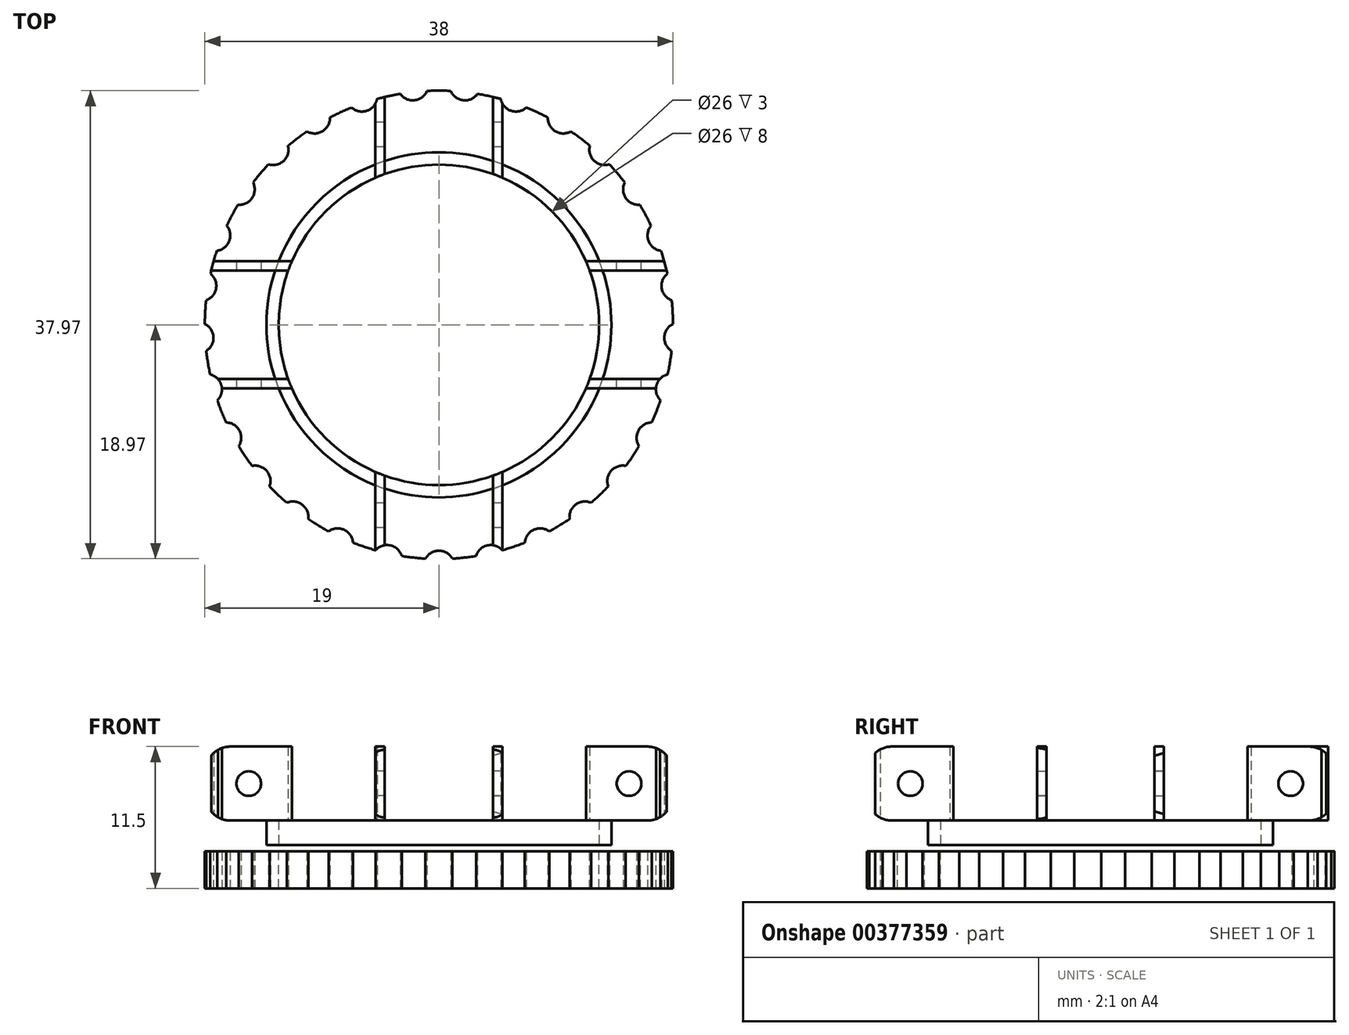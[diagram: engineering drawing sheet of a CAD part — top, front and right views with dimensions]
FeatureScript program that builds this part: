
annotation { "Feature Type Name" : "Feature", "Feature Type Description" : "" }
export const myFeature = defineFeature(function(context is Context, id is Id, definition is map)
    precondition{}
    {
        {
            var Q0;
            Q0=qCreatedBy(makeId("Top.planeOp"),FACE);
            var sketch = newSketch(context, id + "F0", { "sketchPlane" : qUnion([Q0])});
            skCircle(sketch, "E0", {"center": v(0, 0) * mm, "radius": 11 * mm});
            skArc(sketch, "E1.0", {"start": v(-5.15, 11.93) * mm, "mid": v(-9.2, 9.2) * mm, "end": v(-11.93, 5.15) * mm});
            skLineSegment(sketch, "E2.bottom", {"start": v(-4.4, 18.93) * mm, "end": v(-5.8, 18.93) * mm});
            skLineSegment(sketch, "E2.top", {"start": v(-4.4, 18.93) * mm, "end": v(-5.8, 18.93) * mm});
            skLineSegment(sketch, "E2.left", {"start": v(-4.4, 18.93) * mm, "end": v(-4.4, 18.93) * mm});
            skLineSegment(sketch, "E2.right", {"start": v(-5.8, 18.93) * mm, "end": v(-5.8, 18.93) * mm});
            skLineSegment(sketch, "E3.bottom", {"start": v(-4.4, 18.93) * mm, "end": v(-5.15, 18.93) * mm});
            skLineSegment(sketch, "E3.left", {"start": v(-4.4, 18.93) * mm, "end": v(-4.4, 12.23) * mm});
            skLineSegment(sketch, "E3.right", {"start": v(-5.15, 18.93) * mm, "end": v(-5.15, 11.93) * mm});
            skLineSegment(sketch, "E4.bottom", {"start": v(5.15, 18.93) * mm, "end": v(4.4, 18.93) * mm});
            skLineSegment(sketch, "E4.left", {"start": v(5.15, 18.93) * mm, "end": v(5.15, 11.93) * mm});
            skLineSegment(sketch, "E4.right", {"start": v(4.4, 18.93) * mm, "end": v(4.4, 12.23) * mm});
            skPoint(sketch, "E5.orphan", {"position": v(-5.15, 11.36) * mm});
            skArc(sketch, "E6.trimOffspring", {"start": v(4.4, 12.23) * mm, "mid": v(0, 13) * mm, "end": v(-4.4, 12.23) * mm});
            skPoint(sketch, "E4.top.end.orphan", {"position": v(4.4, 11.36) * mm});
            skLineSegment(sketch, "E7.bottom", {"start": v(-18.93, 5.15) * mm, "end": v(-11.93, 5.15) * mm});
            skLineSegment(sketch, "E7.top", {"start": v(-18.93, 4.4) * mm, "end": v(-12.23, 4.4) * mm});
            skLineSegment(sketch, "E7.left", {"start": v(-18.93, 5.15) * mm, "end": v(-18.93, 4.4) * mm});
            skLineSegment(sketch, "E8.bottom", {"start": v(-18.93, -5.15) * mm, "end": v(-11.93, -5.15) * mm});
            skLineSegment(sketch, "E8.top", {"start": v(-18.93, -4.4) * mm, "end": v(-12.23, -4.4) * mm});
            skLineSegment(sketch, "E8.left", {"start": v(-18.93, -5.15) * mm, "end": v(-18.93, -4.4) * mm});
            skLineSegment(sketch, "E9.bottom", {"start": v(-5.15, -18.93) * mm, "end": v(-4.4, -18.93) * mm});
            skLineSegment(sketch, "E9.left", {"start": v(-5.15, -18.93) * mm, "end": v(-5.15, -11.93) * mm});
            skLineSegment(sketch, "E9.right", {"start": v(-4.4, -18.93) * mm, "end": v(-4.4, -12.23) * mm});
            skLineSegment(sketch, "E10.bottom", {"start": v(5.15, -18.93) * mm, "end": v(4.4, -18.93) * mm});
            skLineSegment(sketch, "E10.left", {"start": v(5.15, -18.93) * mm, "end": v(5.15, -11.93) * mm});
            skLineSegment(sketch, "E10.right", {"start": v(4.4, -18.93) * mm, "end": v(4.4, -12.23) * mm});
            skLineSegment(sketch, "E11.bottom", {"start": v(18.93, -5.15) * mm, "end": v(11.93, -5.15) * mm});
            skLineSegment(sketch, "E11.top", {"start": v(18.93, -4.4) * mm, "end": v(12.23, -4.4) * mm});
            skLineSegment(sketch, "E11.left", {"start": v(18.93, -5.15) * mm, "end": v(18.93, -4.4) * mm});
            skLineSegment(sketch, "E12.bottom", {"start": v(18.93, 5.15) * mm, "end": v(11.93, 5.15) * mm});
            skLineSegment(sketch, "E12.top", {"start": v(18.93, 4.4) * mm, "end": v(12.23, 4.4) * mm});
            skLineSegment(sketch, "E12.left", {"start": v(18.93, 5.15) * mm, "end": v(18.93, 4.4) * mm});
            skPoint(sketch, "E13.orphan", {"position": v(-10.92, 4.4) * mm});
            skArc(sketch, "E14.trimOffspring", {"start": v(-12.23, 4.4) * mm, "mid": v(-13, 0) * mm, "end": v(-12.23, -4.4) * mm});
            skArc(sketch, "E15.trimOffspring", {"start": v(-11.93, -5.15) * mm, "mid": v(-9.2, -9.2) * mm, "end": v(-5.15, -11.93) * mm});
            skPoint(sketch, "E8.right.end.orphan", {"position": v(-10.92, -4.4) * mm});
            skPoint(sketch, "E16.orphan", {"position": v(10.83, 4.4) * mm});
            skArc(sketch, "E17.trimOffspring", {"start": v(11.93, 5.15) * mm, "mid": v(9.2, 9.2) * mm, "end": v(5.15, 11.93) * mm});
            skPoint(sketch, "E11.right.end.orphan", {"position": v(10.93, -4.4) * mm});
            skArc(sketch, "E18.trimOffspring", {"start": v(12.23, -4.4) * mm, "mid": v(13, 0) * mm, "end": v(12.23, 4.4) * mm});
            skArc(sketch, "E19.trimOffspring", {"start": v(5.15, -11.93) * mm, "mid": v(9.2, -9.2) * mm, "end": v(11.93, -5.15) * mm});
            skPoint(sketch, "E20.orphan", {"position": v(4.4, -10.83) * mm});
            skPoint(sketch, "E9.top.end.orphan", {"position": v(-4.4, -10.9) * mm});
            skArc(sketch, "E21.trimOffspring", {"start": v(-4.4, -12.23) * mm, "mid": v(0, -13) * mm, "end": v(4.4, -12.23) * mm});
            skSolve(sketch);
        }
        {
            var Q0;
            Q0=makeQuery(id+"F0.imprint","IMPRINT",FACE,{"disambiguationData":[TD([[makeQuery(id+"F0.imprint","IMPRINT",EDGE,{"derivedFrom":sQuery(id+"F0.wireOp",EDGE,"E0")}),-1.0]])]});
            extrude(context, id + "F1", {"entities" : qUnion([Q0]), "depth" : 6 * mm});
        }
        {
            var Q0;
            Q0=makeQuery(id+"F1.opExtrude","CAP_EDGE",EDGE,{"disambiguationData":[OSD([sQuery(id+"F0.wireOp",EDGE,"E9.bottom")])],"isStart":true});
            var Q1;
            Q1=makeQuery(id+"F1.opExtrude","CAP_EDGE",EDGE,{"disambiguationData":[OSD([sQuery(id+"F0.wireOp",EDGE,"E9.bottom")])],"isStart":false});
            var Q2;
            Q2=makeQuery(id+"F1.opExtrude","CAP_EDGE",EDGE,{"disambiguationData":[OSD([sQuery(id+"F0.wireOp",EDGE,"E10.bottom")])],"isStart":true});
            var Q3;
            Q3=makeQuery(id+"F1.opExtrude","CAP_EDGE",EDGE,{"disambiguationData":[OSD([sQuery(id+"F0.wireOp",EDGE,"E10.bottom")])],"isStart":false});
            var Q4;
            Q4=makeQuery(id+"F1.opExtrude","CAP_EDGE",EDGE,{"disambiguationData":[OSD([sQuery(id+"F0.wireOp",EDGE,"E8.left")])],"isStart":true});
            var Q5;
            Q5=makeQuery(id+"F1.opExtrude","CAP_EDGE",EDGE,{"disambiguationData":[OSD([sQuery(id+"F0.wireOp",EDGE,"E8.left")])],"isStart":false});
            var Q6;
            Q6=makeQuery(id+"F1.opExtrude","CAP_EDGE",EDGE,{"disambiguationData":[OSD([sQuery(id+"F0.wireOp",EDGE,"E7.left")])],"isStart":true});
            var Q7;
            Q7=makeQuery(id+"F1.opExtrude","CAP_EDGE",EDGE,{"disambiguationData":[OSD([sQuery(id+"F0.wireOp",EDGE,"E7.left")])],"isStart":false});
            var Q8;
            Q8=makeQuery(id+"F1.opExtrude","CAP_EDGE",EDGE,{"disambiguationData":[OSD([sQuery(id+"F0.wireOp",EDGE,"E3.bottom")])],"isStart":true});
            var Q9;
            Q9=makeQuery(id+"F1.opExtrude","CAP_EDGE",EDGE,{"disambiguationData":[OSD([sQuery(id+"F0.wireOp",EDGE,"E3.bottom")])],"isStart":false});
            var Q10;
            Q10=makeQuery(id+"F1.opExtrude","CAP_EDGE",EDGE,{"disambiguationData":[OSD([sQuery(id+"F0.wireOp",EDGE,"E4.bottom")])],"isStart":true});
            var Q11;
            Q11=makeQuery(id+"F1.opExtrude","CAP_EDGE",EDGE,{"disambiguationData":[OSD([sQuery(id+"F0.wireOp",EDGE,"E4.bottom")])],"isStart":false});
            var Q12;
            Q12=makeQuery(id+"F1.opExtrude","CAP_EDGE",EDGE,{"disambiguationData":[OSD([sQuery(id+"F0.wireOp",EDGE,"E12.left")])],"isStart":true});
            var Q13;
            Q13=makeQuery(id+"F1.opExtrude","CAP_EDGE",EDGE,{"disambiguationData":[OSD([sQuery(id+"F0.wireOp",EDGE,"E12.left")])],"isStart":false});
            var Q14;
            Q14=makeQuery(id+"F1.opExtrude","CAP_EDGE",EDGE,{"disambiguationData":[OSD([sQuery(id+"F0.wireOp",EDGE,"E11.left")])],"isStart":true});
            var Q15;
            Q15=makeQuery(id+"F1.opExtrude","CAP_EDGE",EDGE,{"disambiguationData":[OSD([sQuery(id+"F0.wireOp",EDGE,"E11.left")])],"isStart":false});
            fillet(context, id + "F2", {"entities" : qUnion([Q0, Q1, Q2, Q3, Q4, Q5, Q6, Q7, Q8, Q9, Q10, Q11, Q12, Q13, Q14, Q15]), "radius" : 2 * mm, "tangentPropagation" : true, "allowEdgeOverflow" : false});
        }
        {
            var Q0;
            Q0=makeQuery(id+"F1.opExtrude","SWEPT_FACE",FACE,{"disambiguationData":[OSD([sQuery(id+"F0.wireOp",EDGE,"E8.bottom")])]});
            var sketch = newSketch(context, id + "F3", { "sketchPlane" : qUnion([Q0])});
            skLineSegment(sketch, "E22", {"start": v(-18.93, 3) * mm, "end": v(-11.93, 3) * mm, "construction": true});
            skCircle(sketch, "E23", {"center": v(-15.43, 3) * mm, "radius": 1 * mm});
            skSolve(sketch);
        }
        {
            var Q0;
            Q0=makeQuery(id+"F1.opExtrude","SWEPT_FACE",FACE,{"disambiguationData":[OSD([sQuery(id+"F0.wireOp",EDGE,"E10.left")])]});
            var sketch = newSketch(context, id + "F4", { "sketchPlane" : qUnion([Q0])});
            skLineSegment(sketch, "E24", {"start": v(-18.93, 3) * mm, "end": v(-11.93, 3) * mm, "construction": true});
            skCircle(sketch, "E25", {"center": v(-15.43, 3) * mm, "radius": 1 * mm});
            skSolve(sketch);
        }
        {
            var Q0;
            Q0=makeQuery(id+"F1.opExtrude","SWEPT_FACE",FACE,{"disambiguationData":[OSD([sQuery(id+"F0.wireOp",EDGE,"E12.bottom")])]});
            var sketch = newSketch(context, id + "F5", { "sketchPlane" : qUnion([Q0])});
            skLineSegment(sketch, "E26", {"start": v(-18.93, 3) * mm, "end": v(-11.93, 3) * mm, "construction": true});
            skCircle(sketch, "E27", {"center": v(-15.43, 3) * mm, "radius": 1 * mm});
            skSolve(sketch);
        }
        {
            var Q0;
            Q0=makeQuery(id+"F1.opExtrude","SWEPT_FACE",FACE,{"disambiguationData":[OSD([sQuery(id+"F0.wireOp",EDGE,"E3.right")])]});
            var sketch = newSketch(context, id + "F6", { "sketchPlane" : qUnion([Q0])});
            skLineSegment(sketch, "E28", {"start": v(-18.93, 3) * mm, "end": v(-11.93, 3) * mm, "construction": true});
            skCircle(sketch, "E29", {"center": v(-15.43, 3) * mm, "radius": 1 * mm});
            skSolve(sketch);
        }
        {
            var Q0;
            Q0=makeQuery(id+"F6.imprint","IMPRINT",FACE,{"disambiguationData":[TD([[makeQuery(id+"F6.imprint","IMPRINT",EDGE,{"derivedFrom":sQuery(id+"F6.wireOp",EDGE,"E29")}),1.0]])]});
            extrude(context, id + "F7", {"entities" : qUnion([Q0]), "operationType" : NewBodyOperationType.REMOVE, "endBound" : BoundingType.THROUGH_ALL, "oppositeDirection" : true, "depth" : 25 * mm});
        }
        {
            var Q0;
            Q0=qSketchRegion(id+"F5",true);
            extrude(context, id + "F8", {"entities" : qUnion([Q0]), "operationType" : NewBodyOperationType.REMOVE, "endBound" : BoundingType.THROUGH_ALL, "oppositeDirection" : true, "depth" : 25 * mm});
        }
        {
            var Q0;
            Q0=qSketchRegion(id+"F4",true);
            extrude(context, id + "F9", {"entities" : qUnion([Q0]), "operationType" : NewBodyOperationType.REMOVE, "endBound" : BoundingType.THROUGH_ALL, "oppositeDirection" : true, "depth" : 25 * mm});
        }
        {
            var Q0;
            Q0=qSketchRegion(id+"F3",true);
            extrude(context, id + "F10", {"entities" : qUnion([Q0]), "operationType" : NewBodyOperationType.REMOVE, "endBound" : BoundingType.THROUGH_ALL, "oppositeDirection" : true, "depth" : 25 * mm});
        }
        {
            var Q0;
            Q0=makeQuery(id+"F1.opExtrude","CAP_FACE",FACE,{"disambiguationData":[OSD([sQuery(id+"F0.wireOp",EDGE,"E0"),sQuery(id+"F0.wireOp",EDGE,"E1.0"),sQuery(id+"F0.wireOp",EDGE,"E3.bottom"),sQuery(id+"F0.wireOp",EDGE,"E3.left"),sQuery(id+"F0.wireOp",EDGE,"E3.right"),sQuery(id+"F0.wireOp",EDGE,"E4.bottom"),sQuery(id+"F0.wireOp",EDGE,"E4.left"),sQuery(id+"F0.wireOp",EDGE,"E4.right"),sQuery(id+"F0.wireOp",EDGE,"E6.trimOffspring"),sQuery(id+"F0.wireOp",EDGE,"E7.bottom"),sQuery(id+"F0.wireOp",EDGE,"E7.top"),sQuery(id+"F0.wireOp",EDGE,"E7.left"),sQuery(id+"F0.wireOp",EDGE,"E8.bottom"),sQuery(id+"F0.wireOp",EDGE,"E8.top"),sQuery(id+"F0.wireOp",EDGE,"E8.left"),sQuery(id+"F0.wireOp",EDGE,"E9.bottom"),sQuery(id+"F0.wireOp",EDGE,"E9.left"),sQuery(id+"F0.wireOp",EDGE,"E9.right"),sQuery(id+"F0.wireOp",EDGE,"E10.bottom"),sQuery(id+"F0.wireOp",EDGE,"E10.left"),sQuery(id+"F0.wireOp",EDGE,"E10.right"),sQuery(id+"F0.wireOp",EDGE,"E11.bottom"),sQuery(id+"F0.wireOp",EDGE,"E11.top"),sQuery(id+"F0.wireOp",EDGE,"E11.left"),sQuery(id+"F0.wireOp",EDGE,"E12.bottom"),sQuery(id+"F0.wireOp",EDGE,"E12.top"),sQuery(id+"F0.wireOp",EDGE,"E12.left"),sQuery(id+"F0.wireOp",EDGE,"E14.trimOffspring"),sQuery(id+"F0.wireOp",EDGE,"E15.trimOffspring"),sQuery(id+"F0.wireOp",EDGE,"E17.trimOffspring"),sQuery(id+"F0.wireOp",EDGE,"E18.trimOffspring"),sQuery(id+"F0.wireOp",EDGE,"E19.trimOffspring"),sQuery(id+"F0.wireOp",EDGE,"E21.trimOffspring")])],"isStart":true});
            var sketch = newSketch(context, id + "F11", { "sketchPlane" : qUnion([Q0])});
            skCircle(sketch, "E30.0", {"center": v(0, 0) * mm, "radius": 11 * mm});
            skCircle(sketch, "E31", {"center": v(0, 0) * mm, "radius": 14 * mm});
            skCircle(sketch, "E32", {"center": v(0, 0) * mm, "radius": 13 * mm});
            skSolve(sketch);
        }
        {
            var Q0;
            Q0=makeQuery(id+"F11.imprint","IMPRINT",FACE,{"disambiguationData":[TD([[makeQuery(id+"F11.imprint","IMPRINT",EDGE,{"derivedFrom":sQuery(id+"F11.wireOp",EDGE,"E30.0")}),1.0]])]});
            var Q1;
            {var subQ0=sQuery(id+"F11.wireOp",EDGE,"E31");var subQ1=makeQuery(id+"F1.opExtrude","CAP_EDGE",EDGE,{"disambiguationData":[OSD([sQuery(id+"F0.wireOp",EDGE,"E9.left")])],"isStart":true});var subQ2=makeQuery(id+"F11.imprint","INTERSECT",VERTEX,{"derivedFrom":[subQ1,subQ0]});Q1=makeQuery(id+"F11.imprint","IMPRINT",FACE,{"disambiguationData":[TD([[makeQuery(id+"F11.imprint","IMPRINT",EDGE,{"disambiguationData":[TD([[subQ2,-1.0]])],"derivedFrom":subQ0}),1.0]])]});}
            var Q2;
            {var subQ0=sQuery(id+"F11.wireOp",EDGE,"E31");var subQ1=makeQuery(id+"F1.opExtrude","CAP_EDGE",EDGE,{"disambiguationData":[OSD([sQuery(id+"F0.wireOp",EDGE,"E10.right")])],"isStart":true});var subQ2=makeQuery(id+"F11.imprint","INTERSECT",VERTEX,{"derivedFrom":[subQ1,subQ0]});Q2=makeQuery(id+"F11.imprint","IMPRINT",FACE,{"disambiguationData":[TD([[makeQuery(id+"F11.imprint","IMPRINT",EDGE,{"disambiguationData":[TD([[subQ2,-1.0]])],"derivedFrom":subQ0}),1.0]])]});}
            var Q3;
            {var subQ0=sQuery(id+"F11.wireOp",EDGE,"E31");var subQ1=makeQuery(id+"F1.opExtrude","CAP_EDGE",EDGE,{"disambiguationData":[OSD([sQuery(id+"F0.wireOp",EDGE,"E11.bottom")])],"isStart":true});var subQ2=makeQuery(id+"F11.imprint","INTERSECT",VERTEX,{"derivedFrom":[subQ1,subQ0]});Q3=makeQuery(id+"F11.imprint","IMPRINT",FACE,{"disambiguationData":[TD([[makeQuery(id+"F11.imprint","IMPRINT",EDGE,{"disambiguationData":[TD([[subQ2,-1.0]])],"derivedFrom":subQ0}),1.0]])]});}
            var Q4;
            {var subQ0=sQuery(id+"F11.wireOp",EDGE,"E31");var subQ1=makeQuery(id+"F1.opExtrude","CAP_EDGE",EDGE,{"disambiguationData":[OSD([sQuery(id+"F0.wireOp",EDGE,"E11.top")])],"isStart":true});var subQ2=makeQuery(id+"F11.imprint","INTERSECT",VERTEX,{"derivedFrom":[subQ1,subQ0]});Q4=makeQuery(id+"F11.imprint","IMPRINT",FACE,{"disambiguationData":[TD([[makeQuery(id+"F11.imprint","IMPRINT",EDGE,{"disambiguationData":[TD([[subQ2,1.0]])],"derivedFrom":subQ0}),1.0]])]});}
            var Q5;
            {var subQ0=sQuery(id+"F11.wireOp",EDGE,"E31");var subQ1=makeQuery(id+"F1.opExtrude","CAP_EDGE",EDGE,{"disambiguationData":[OSD([sQuery(id+"F0.wireOp",EDGE,"E4.left")])],"isStart":true});var subQ2=makeQuery(id+"F11.imprint","INTERSECT",VERTEX,{"derivedFrom":[subQ1,subQ0]});Q5=makeQuery(id+"F11.imprint","IMPRINT",FACE,{"disambiguationData":[TD([[makeQuery(id+"F11.imprint","IMPRINT",EDGE,{"disambiguationData":[TD([[subQ2,-1.0]])],"derivedFrom":subQ0}),1.0]])]});}
            var Q6;
            {var subQ0=sQuery(id+"F11.wireOp",EDGE,"E31");var subQ1=makeQuery(id+"F1.opExtrude","CAP_EDGE",EDGE,{"disambiguationData":[OSD([sQuery(id+"F0.wireOp",EDGE,"E3.left")])],"isStart":true});var subQ2=makeQuery(id+"F11.imprint","INTERSECT",VERTEX,{"derivedFrom":[subQ1,subQ0]});Q6=makeQuery(id+"F11.imprint","IMPRINT",FACE,{"disambiguationData":[TD([[makeQuery(id+"F11.imprint","IMPRINT",EDGE,{"disambiguationData":[TD([[subQ2,-1.0]])],"derivedFrom":subQ0}),1.0]])]});}
            var Q7;
            {var subQ0=sQuery(id+"F11.wireOp",EDGE,"E31");var subQ1=makeQuery(id+"F1.opExtrude","CAP_EDGE",EDGE,{"disambiguationData":[OSD([sQuery(id+"F0.wireOp",EDGE,"E7.bottom")])],"isStart":true});var subQ2=makeQuery(id+"F11.imprint","INTERSECT",VERTEX,{"derivedFrom":[subQ1,subQ0]});Q7=makeQuery(id+"F11.imprint","IMPRINT",FACE,{"disambiguationData":[TD([[makeQuery(id+"F11.imprint","IMPRINT",EDGE,{"disambiguationData":[TD([[subQ2,-1.0]])],"derivedFrom":subQ0}),1.0]])]});}
            var Q8;
            {var subQ0=sQuery(id+"F11.wireOp",EDGE,"E31");var subQ1=makeQuery(id+"F1.opExtrude","CAP_EDGE",EDGE,{"disambiguationData":[OSD([sQuery(id+"F0.wireOp",EDGE,"E8.top")])],"isStart":true});var subQ2=makeQuery(id+"F11.imprint","INTERSECT",VERTEX,{"derivedFrom":[subQ1,subQ0]});Q8=makeQuery(id+"F11.imprint","IMPRINT",FACE,{"disambiguationData":[TD([[makeQuery(id+"F11.imprint","IMPRINT",EDGE,{"disambiguationData":[TD([[subQ2,-1.0]])],"derivedFrom":subQ0}),1.0]])]});}
            var Q9;
            {var subQ0=sQuery(id+"F11.wireOp",EDGE,"E31");var subQ1=makeQuery(id+"F1.opExtrude","CAP_EDGE",EDGE,{"disambiguationData":[OSD([sQuery(id+"F0.wireOp",EDGE,"E9.right")])],"isStart":true});var subQ2=makeQuery(id+"F11.imprint","INTERSECT",VERTEX,{"derivedFrom":[subQ1,subQ0]});Q9=makeQuery(id+"F11.imprint","IMPRINT",FACE,{"disambiguationData":[TD([[makeQuery(id+"F11.imprint","IMPRINT",EDGE,{"disambiguationData":[TD([[subQ2,-1.0]])],"derivedFrom":subQ0}),1.0]])]});}
            var Q10;
            {var subQ0=sQuery(id+"F11.wireOp",EDGE,"E31");var subQ1=makeQuery(id+"F1.opExtrude","CAP_EDGE",EDGE,{"disambiguationData":[OSD([sQuery(id+"F0.wireOp",EDGE,"E10.left")])],"isStart":true});var subQ2=makeQuery(id+"F11.imprint","INTERSECT",VERTEX,{"derivedFrom":[subQ1,subQ0]});Q10=makeQuery(id+"F11.imprint","IMPRINT",FACE,{"disambiguationData":[TD([[makeQuery(id+"F11.imprint","IMPRINT",EDGE,{"disambiguationData":[TD([[subQ2,-1.0]])],"derivedFrom":subQ0}),1.0]])]});}
            var Q11;
            {var subQ0=sQuery(id+"F11.wireOp",EDGE,"E31");var subQ1=makeQuery(id+"F1.opExtrude","CAP_EDGE",EDGE,{"disambiguationData":[OSD([sQuery(id+"F0.wireOp",EDGE,"E11.bottom")])],"isStart":true});var subQ2=makeQuery(id+"F11.imprint","INTERSECT",VERTEX,{"derivedFrom":[subQ1,subQ0]});Q11=makeQuery(id+"F11.imprint","IMPRINT",FACE,{"disambiguationData":[TD([[makeQuery(id+"F11.imprint","IMPRINT",EDGE,{"disambiguationData":[TD([[subQ2,1.0]])],"derivedFrom":subQ0}),1.0]])]});}
            var Q12;
            {var subQ0=sQuery(id+"F11.wireOp",EDGE,"E31");var subQ1=makeQuery(id+"F1.opExtrude","CAP_EDGE",EDGE,{"disambiguationData":[OSD([sQuery(id+"F0.wireOp",EDGE,"E12.bottom")])],"isStart":true});var subQ2=makeQuery(id+"F11.imprint","INTERSECT",VERTEX,{"derivedFrom":[subQ1,subQ0]});Q12=makeQuery(id+"F11.imprint","IMPRINT",FACE,{"disambiguationData":[TD([[makeQuery(id+"F11.imprint","IMPRINT",EDGE,{"disambiguationData":[TD([[subQ2,-1.0]])],"derivedFrom":subQ0}),1.0]])]});}
            var Q13;
            {var subQ0=sQuery(id+"F11.wireOp",EDGE,"E31");var subQ1=makeQuery(id+"F1.opExtrude","CAP_EDGE",EDGE,{"disambiguationData":[OSD([sQuery(id+"F0.wireOp",EDGE,"E4.right")])],"isStart":true});var subQ2=makeQuery(id+"F11.imprint","INTERSECT",VERTEX,{"derivedFrom":[subQ1,subQ0]});Q13=makeQuery(id+"F11.imprint","IMPRINT",FACE,{"disambiguationData":[TD([[makeQuery(id+"F11.imprint","IMPRINT",EDGE,{"disambiguationData":[TD([[subQ2,-1.0]])],"derivedFrom":subQ0}),1.0]])]});}
            var Q14;
            {var subQ0=sQuery(id+"F11.wireOp",EDGE,"E31");var subQ1=makeQuery(id+"F1.opExtrude","CAP_EDGE",EDGE,{"disambiguationData":[OSD([sQuery(id+"F0.wireOp",EDGE,"E3.right")])],"isStart":true});var subQ2=makeQuery(id+"F11.imprint","INTERSECT",VERTEX,{"derivedFrom":[subQ1,subQ0]});Q14=makeQuery(id+"F11.imprint","IMPRINT",FACE,{"disambiguationData":[TD([[makeQuery(id+"F11.imprint","IMPRINT",EDGE,{"disambiguationData":[TD([[subQ2,-1.0]])],"derivedFrom":subQ0}),1.0]])]});}
            var Q15;
            {var subQ0=sQuery(id+"F11.wireOp",EDGE,"E31");var subQ1=makeQuery(id+"F1.opExtrude","CAP_EDGE",EDGE,{"disambiguationData":[OSD([sQuery(id+"F0.wireOp",EDGE,"E7.top")])],"isStart":true});var subQ2=makeQuery(id+"F11.imprint","INTERSECT",VERTEX,{"derivedFrom":[subQ1,subQ0]});Q15=makeQuery(id+"F11.imprint","IMPRINT",FACE,{"disambiguationData":[TD([[makeQuery(id+"F11.imprint","IMPRINT",EDGE,{"disambiguationData":[TD([[subQ2,-1.0]])],"derivedFrom":subQ0}),1.0]])]});}
            var Q16;
            {var subQ0=sQuery(id+"F11.wireOp",EDGE,"E31");var subQ1=makeQuery(id+"F1.opExtrude","CAP_EDGE",EDGE,{"disambiguationData":[OSD([sQuery(id+"F0.wireOp",EDGE,"E8.bottom")])],"isStart":true});var subQ2=makeQuery(id+"F11.imprint","INTERSECT",VERTEX,{"derivedFrom":[subQ1,subQ0]});Q16=makeQuery(id+"F11.imprint","IMPRINT",FACE,{"disambiguationData":[TD([[makeQuery(id+"F11.imprint","IMPRINT",EDGE,{"disambiguationData":[TD([[subQ2,-1.0]])],"derivedFrom":subQ0}),1.0]])]});}
            extrude(context, id + "F12", {"entities" : qUnion([Q0, Q1, Q2, Q3, Q4, Q5, Q6, Q7, Q8, Q9, Q10, Q11, Q12, Q13, Q14, Q15, Q16]), "operationType" : NewBodyOperationType.ADD, "depth" : 2 * mm});
        }
        {
            var Q0;
            Q0=makeQuery(id+"F12.opExtrude","CAP_FACE",FACE,{"disambiguationData":[OSD([sQuery(id+"F11.wireOp",EDGE,"E30.0"),sQuery(id+"F11.wireOp",EDGE,"E31")])],"isStart":false});
            var sketch = newSketch(context, id + "F13", { "sketchPlane" : qUnion([Q0])});
            skCircle(sketch, "E33", {"center": v(0, 0) * mm, "radius": 12.5 * mm});
            skCircle(sketch, "E34.0", {"center": v(0, 0) * mm, "radius": 11 * mm});
            skSolve(sketch);
        }
        {
            var Q0;
            Q0=makeQuery(id+"F13.imprint","IMPRINT",FACE,{"disambiguationData":[TD([[makeQuery(id+"F13.imprint","IMPRINT",EDGE,{"derivedFrom":sQuery(id+"F13.wireOp",EDGE,"E33")}),1.0]])]});
            extrude(context, id + "F14", {"entities" : qUnion([Q0]), "operationType" : NewBodyOperationType.ADD, "depth" : 4 * mm});
        }
        {
            var Q0;
            Q0=makeQuery(id+"F14.opExtrude","CAP_FACE",FACE,{"disambiguationData":[OSD([sQuery(id+"F13.wireOp",EDGE,"E33"),sQuery(id+"F13.wireOp",EDGE,"E34.0")])],"isStart":false});
            var sketch = newSketch(context, id + "F15", { "sketchPlane" : qUnion([Q0])});
            skCircle(sketch, "E35.0", {"center": v(0, 0) * mm, "radius": 11 * mm});
            skCircle(sketch, "E36", {"center": v(0, 0) * mm, "radius": 14 * mm});
            skCircle(sketch, "E37", {"center": v(0, 0) * mm, "radius": 13 * mm});
            skSolve(sketch);
        }
        {
            var Q0;
            Q0=makeQuery(id+"F15.imprint","IMPRINT",FACE,{"disambiguationData":[TD([[makeQuery(id+"F15.imprint","IMPRINT",EDGE,{"derivedFrom":sQuery(id+"F15.wireOp",EDGE,"E36")}),1.0]])]});
            var Q1;
            Q1=makeQuery(id+"F15.imprint","IMPRINT",FACE,{"disambiguationData":[TD([[makeQuery(id+"F15.imprint","IMPRINT",EDGE,{"derivedFrom":sQuery(id+"F15.wireOp",EDGE,"E37")}),1.0]])]});
            var Q2;
            Q2=makeQuery(id+"F15.imprint","IMPRINT",FACE,{"disambiguationData":[TD([[makeQuery(id+"F15.imprint","IMPRINT",EDGE,{"derivedFrom":sQuery(id+"F15.wireOp",EDGE,"E35.0")}),1.0]])]});
            extrude(context, id + "F16", {"entities" : qUnion([Q0, Q1, Q2]), "operationType" : NewBodyOperationType.ADD, "depth" : 2 * mm});
        }
        {
            var Q0;
            Q0=makeQuery(id+"F12.opExtrude","CAP_FACE",FACE,{"disambiguationData":[OSD([sQuery(id+"F11.wireOp",EDGE,"E30.0"),sQuery(id+"F11.wireOp",EDGE,"E31")])],"isStart":false});
            cPlane(context, id + "F17", {"entities" : qUnion([Q0]), "cplaneType" : CPlaneType.OFFSET, "offset" : .5 * mm, "width" : 150 * mm, "height" : 150 * mm});
        }
        {
            var Q0;
            Q0=qCreatedBy(id+"F17.planeOp",FACE);
            var sketch = newSketch(context, id + "F18", { "sketchPlane" : qUnion([Q0])});
            skCircle(sketch, "E38", {"center": v(0, 0) * mm, "radius": 19 * mm});
            skCircle(sketch, "E39.0", {"center": v(0, 0) * mm, "radius": 13 * mm});
            skSolve(sketch);
        }
        {
            var Q0;
            Q0 = qSketchRegion(id + "F18", true);
            extrude(context, id + "F19", {"entities" : qUnion([Q0]), "depth" : 3 * mm});
        }
        {
            var Q0;
            Q0=makeQuery(id+"F19.opExtrude","CAP_FACE",FACE,{"disambiguationData":[OSD([sQuery(id+"F18.wireOp",EDGE,"E38"),sQuery(id+"F18.wireOp",EDGE,"E39.0")])],"isStart":false});
            var sketch = newSketch(context, id + "F20", { "sketchPlane" : qUnion([Q0])});
            skCircle(sketch, "E40", {"center": v(0, 19.58) * mm, "radius": 1.25 * mm});
            skCircle(sketch, "E41.1.0", {"center": v(-4.2, 19.12) * mm, "radius": 1.25 * mm});
            skCircle(sketch, "E41.2.0", {"center": v(-8.22, 17.77) * mm, "radius": 1.25 * mm});
            skCircle(sketch, "E41.3.0", {"center": v(-11.85, 15.58) * mm, "radius": 1.25 * mm});
            skCircle(sketch, "E41.4.0", {"center": v(-14.92, 12.67) * mm, "radius": 1.25 * mm});
            skCircle(sketch, "E41.5.0", {"center": v(-17.3, 9.17) * mm, "radius": 1.25 * mm});
            skCircle(sketch, "E41.6.0", {"center": v(-18.86, 5.24) * mm, "radius": 1.25 * mm});
            skCircle(sketch, "E41.7.0", {"center": v(-19.55, 1.06) * mm, "radius": 1.25 * mm});
            skCircle(sketch, "E41.8.0", {"center": v(-19.32, -3.17) * mm, "radius": 1.25 * mm});
            skCircle(sketch, "E41.9.0", {"center": v(-18.19, -7.25) * mm, "radius": 1.25 * mm});
            skCircle(sketch, "E41.10.0", {"center": v(-16.2, -10.99) * mm, "radius": 1.25 * mm});
            skCircle(sketch, "E41.11.0", {"center": v(-13.46, -14.21) * mm, "radius": 1.25 * mm});
            skCircle(sketch, "E41.12.0", {"center": v(-10.1, -16.77) * mm, "radius": 1.25 * mm});
            skCircle(sketch, "E41.13.0", {"center": v(-6.25, -18.55) * mm, "radius": 1.25 * mm});
            skCircle(sketch, "E41.14.0", {"center": v(-2.12, -19.46) * mm, "radius": 1.25 * mm});
            skCircle(sketch, "E41.15.0", {"center": v(2.12, -19.46) * mm, "radius": 1.25 * mm});
            skCircle(sketch, "E41.16.0", {"center": v(6.25, -18.55) * mm, "radius": 1.25 * mm});
            skCircle(sketch, "E41.17.0", {"center": v(10.1, -16.77) * mm, "radius": 1.25 * mm});
            skCircle(sketch, "E41.18.0", {"center": v(13.46, -14.21) * mm, "radius": 1.25 * mm});
            skCircle(sketch, "E41.19.0", {"center": v(16.2, -10.99) * mm, "radius": 1.25 * mm});
            skCircle(sketch, "E41.20.0", {"center": v(18.19, -7.25) * mm, "radius": 1.25 * mm});
            skCircle(sketch, "E41.21.0", {"center": v(19.32, -3.17) * mm, "radius": 1.25 * mm});
            skCircle(sketch, "E41.22.0", {"center": v(19.55, 1.06) * mm, "radius": 1.25 * mm});
            skCircle(sketch, "E41.23.0", {"center": v(18.86, 5.24) * mm, "radius": 1.25 * mm});
            skCircle(sketch, "E41.24.0", {"center": v(17.3, 9.17) * mm, "radius": 1.25 * mm});
            skPoint(sketch, "E41.center", {"position": v(0, 0) * mm});
            skCircle(sketch, "E42.1.25.0", {"center": v(14.92, 12.67) * mm, "radius": 1.25 * mm});
            skCircle(sketch, "E42.1.26.0", {"center": v(11.85, 15.58) * mm, "radius": 1.25 * mm});
            skCircle(sketch, "E43.1.27.0", {"center": v(8.22, 17.77) * mm, "radius": 1.25 * mm});
            skCircle(sketch, "E43.1.28.0", {"center": v(4.2, 19.12) * mm, "radius": 1.25 * mm});
            skSolve(sketch);
        }
        {
            var Q0;
            Q0=makeQuery(id+"F20.imprint","IMPRINT",FACE,{"disambiguationData":[TD([[makeQuery(id+"F20.imprint","IMPRINT",EDGE,{"derivedFrom":makeQuery(id+"F19.opExtrude","CAP_EDGE",EDGE,{"disambiguationData":[OSD([sQuery(id+"F18.wireOp",EDGE,"E39.0")])],"isStart":false})}),-1.0]])]});
            extrude(context, id + "F21", {"entities" : qUnion([Q0]), "operationType" : NewBodyOperationType.INTERSECT, "endBound" : BoundingType.THROUGH_ALL, "oppositeDirection" : true, "depth" : 25 * mm});
        }
    });
